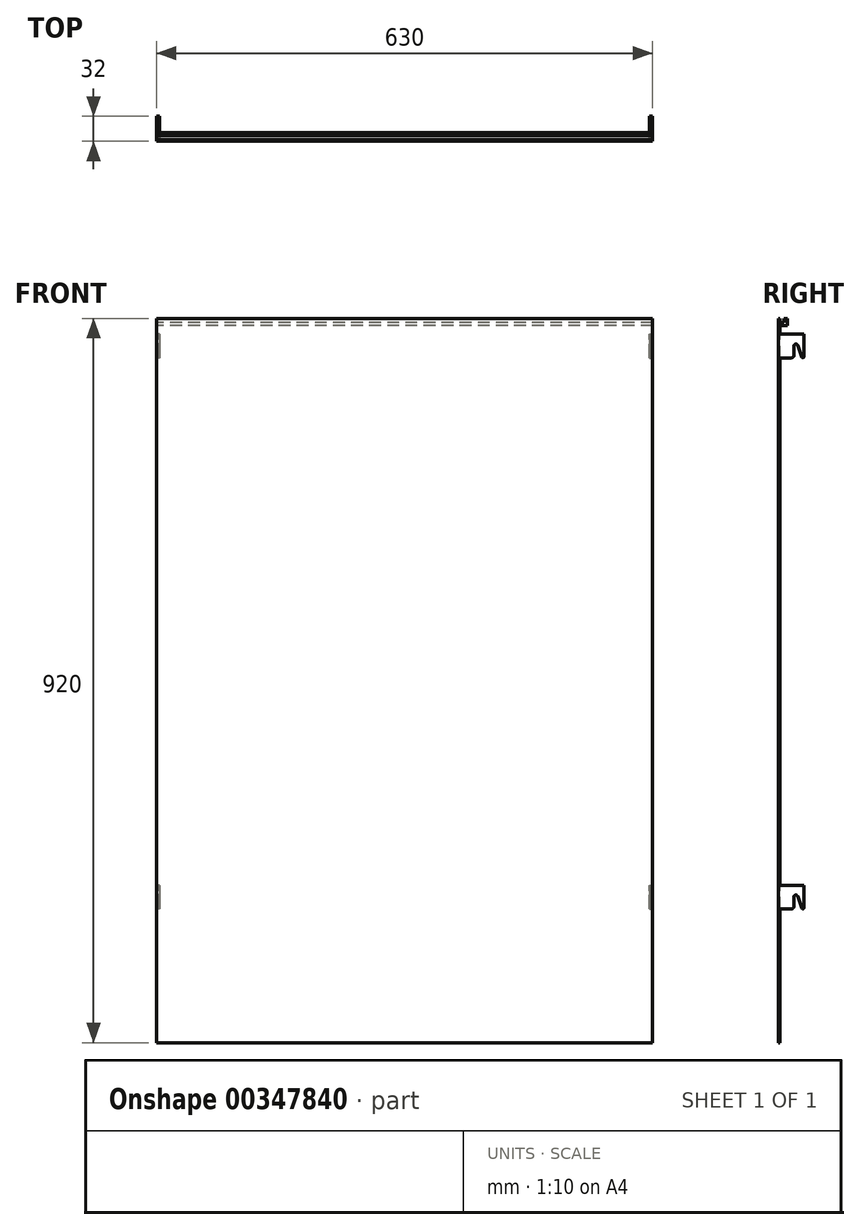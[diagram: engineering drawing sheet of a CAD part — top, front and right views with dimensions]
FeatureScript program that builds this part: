
annotation { "Feature Type Name" : "Feature", "Feature Type Description" : "" }
export const myFeature = defineFeature(function(context is Context, id is Id, definition is map)
    precondition{}
    {
        {
            var Q0;
            Q0=qCreatedBy(makeId("Front.planeOp"),FACE);
            var sketch = newSketch(context, id + "F0", { "sketchPlane" : qUnion([Q0])});
            skLineSegment(sketch, "E0.bottom", {"start": v(315, -460) * mm, "end": v(-315, -460) * mm});
            skLineSegment(sketch, "E0.top", {"start": v(315, 460) * mm, "end": v(-315, 460) * mm});
            skLineSegment(sketch, "E0.left", {"start": v(315, -460) * mm, "end": v(315, 460) * mm});
            skLineSegment(sketch, "E0.right", {"start": v(-315, -460) * mm, "end": v(-315, 460) * mm});
            skPoint(sketch, "E0.middle", {"position": v(0, 0) * mm});
            skLineSegment(sketch, "E1.0", {"start": v(315, 455) * mm, "end": v(-315, 455) * mm});
            skLineSegment(sketch, "E2.0", {"start": v(315, 451) * mm, "end": v(-315, 451) * mm});
            skSolve(sketch);
        }
        {
            var Q0;
            Q0=makeQuery(id+"F0.imprint","IMPRINT",FACE,{"disambiguationData":[TD([[makeQuery(id+"F0.imprint","IMPRINT",EDGE,{"derivedFrom":sQuery(id+"F0.wireOp",EDGE,"E0.bottom")}),-1.0]])]});
            var Q1;
            {var subQ0=sQuery(id+"F0.wireOp",EDGE,"E1.0");Q1=makeQuery(id+"F0.imprint","IMPRINT",FACE,{"disambiguationData":[TD([[makeQuery(id+"F0.imprint","IMPRINT",EDGE,{"derivedFrom":subQ0}),1.0]])]});}
            var Q2;
            {var subQ0=sQuery(id+"F0.wireOp",EDGE,"E0.top");Q2=makeQuery(id+"F0.imprint","IMPRINT",FACE,{"disambiguationData":[TD([[makeQuery(id+"F0.imprint","IMPRINT",EDGE,{"derivedFrom":subQ0}),1.0]])]});}
            extrude(context, id + "F1", {"entities" : qUnion([Q0, Q1, Q2]), "depth" : 2 * mm});
        }
        {
            var Q0;
            Q0=qCreatedBy(makeId("Right.planeOp"),FACE);
            cPlane(context, id + "F2", {"entities" : qUnion([Q0]), "cplaneType" : CPlaneType.OFFSET, "offset" : 315 * mm, "oppositeDirection" : true, "width" : 150 * mm, "height" : 150 * mm});
        }
        {
            var Q0;
            Q0=qCreatedBy(id+"F2.planeOp",FACE);
            var sketch = newSketch(context, id + "F3", { "sketchPlane" : qUnion([Q0])});
            skLineSegment(sketch, "E3", {"start": v(0, 0) * mm, "end": v(0, 440) * mm});
            skLineSegment(sketch, "E4", {"start": v(0, 440) * mm, "end": v(30, 440) * mm});
            skLineSegment(sketch, "E5", {"start": v(30, 440) * mm, "end": v(30, 410.95) * mm});
            skLineSegment(sketch, "E6", {"start": v(29.05, 410) * mm, "end": v(28.67, 410) * mm});
            skLineSegment(sketch, "E7", {"start": v(28, 410) * mm, "end": v(20, 410) * mm});
            skLineSegment(sketch, "E8", {"start": v(20, 410) * mm, "end": v(20, 425) * mm});
            skCircle(sketch, "E9", {"center": v(20, 425) * mm, "radius": 2.5 * mm});
            skLineSegment(sketch, "E10", {"start": v(27.77, 410.63) * mm, "end": v(22.35, 425.84) * mm});
            skLineSegment(sketch, "E11", {"start": v(17.5, 425) * mm, "end": v(17.5, 413) * mm});
            skLineSegment(sketch, "E12", {"start": v(14.5, 410) * mm, "end": v(0, 410) * mm});
            skPoint(sketch, "E13.visualSharp", {"position": v(17.5, 410) * mm});
            skArc(sketch, "E13.filletArc", {"start": v(14.5, 410) * mm, "mid": v(16.62, 410.88) * mm, "end": v(17.5, 413) * mm});
            skPoint(sketch, "E14.visualSharp", {"position": v(28, 410) * mm});
            skArc(sketch, "E14.filletArc", {"start": v(27.77, 410.63) * mm, "mid": v(28.12, 410.17) * mm, "end": v(28.67, 410) * mm});
            skPoint(sketch, "E15.visualSharp", {"position": v(30, 410) * mm});
            skArc(sketch, "E15.filletArc", {"start": v(29.05, 410) * mm, "mid": v(29.72, 410.28) * mm, "end": v(30, 410.95) * mm});
            skSolve(sketch);
        }
        {
            var Q0;
            {var subQ4=sQuery(id+"F3.wireOp",EDGE,"E4");Q0=makeQuery(id+"F3.imprint","IMPRINT",FACE,{"disambiguationData":[TD([[makeQuery(id+"F3.imprint","IMPRINT",EDGE,{"derivedFrom":subQ4}),-1.0]])]});}
            extrude(context, id + "F4", {"entities" : qUnion([Q0]), "depth" : 4 * mm});
        }
        {
            var Q0;
            Q0=makeQuery(id+"F4.opExtrude","SWEPT_BODY",BODY,{"disambiguationData":[OSD([sQuery(id+"F3.wireOp",EDGE,"E3"),sQuery(id+"F3.wireOp",EDGE,"E4"),sQuery(id+"F3.wireOp",EDGE,"E5"),sQuery(id+"F3.wireOp",EDGE,"E6"),sQuery(id+"F3.wireOp",EDGE,"E9"),sQuery(id+"F3.wireOp",EDGE,"E10"),sQuery(id+"F3.wireOp",EDGE,"E11"),sQuery(id+"F3.wireOp",EDGE,"E12"),sQuery(id+"F3.wireOp",EDGE,"E13.filletArc"),sQuery(id+"F3.wireOp",EDGE,"E14.filletArc"),sQuery(id+"F3.wireOp",EDGE,"E15.filletArc")])]});
            transform(context, id + "F5", {"entities" : qUnion([Q0]), "transformType" : TransformType.TRANSLATION_3D, "dx" : 0 * mm, "dy" : 0 * mm, "dz" : -700 * mm, "makeCopy" : true});
        }
        {
            var Q0;
            Q0=makeQuery(id+"F4.opExtrude","SWEPT_BODY",BODY,{"disambiguationData":[OSD([sQuery(id+"F3.wireOp",EDGE,"E3"),sQuery(id+"F3.wireOp",EDGE,"E4"),sQuery(id+"F3.wireOp",EDGE,"E5"),sQuery(id+"F3.wireOp",EDGE,"E6"),sQuery(id+"F3.wireOp",EDGE,"E9"),sQuery(id+"F3.wireOp",EDGE,"E10"),sQuery(id+"F3.wireOp",EDGE,"E11"),sQuery(id+"F3.wireOp",EDGE,"E12"),sQuery(id+"F3.wireOp",EDGE,"E13.filletArc"),sQuery(id+"F3.wireOp",EDGE,"E14.filletArc"),sQuery(id+"F3.wireOp",EDGE,"E15.filletArc")])]});
            var Q1;
            Q1=makeQuery(id+"F5.opPattern","COPY",BODY,{"derivedFrom":makeQuery(id+"F4.opExtrude","SWEPT_BODY",BODY,{"disambiguationData":[OSD([sQuery(id+"F3.wireOp",EDGE,"E3"),sQuery(id+"F3.wireOp",EDGE,"E4"),sQuery(id+"F3.wireOp",EDGE,"E5"),sQuery(id+"F3.wireOp",EDGE,"E6"),sQuery(id+"F3.wireOp",EDGE,"E9"),sQuery(id+"F3.wireOp",EDGE,"E10"),sQuery(id+"F3.wireOp",EDGE,"E11"),sQuery(id+"F3.wireOp",EDGE,"E12"),sQuery(id+"F3.wireOp",EDGE,"E13.filletArc"),sQuery(id+"F3.wireOp",EDGE,"E14.filletArc"),sQuery(id+"F3.wireOp",EDGE,"E15.filletArc")])]}),"instanceName":"1"});
            var Q2;
            Q2=qCreatedBy(makeId("Right.planeOp"),FACE);
            mirror(context, id + "F6", {"operationType" : NewBodyOperationType.ADD, "entities" : qUnion([Q0, Q1]), "mirrorPlane" : qUnion([Q2])});
        }
        {
            var Q0;
            {var subQ0=sQuery(id+"F0.wireOp",EDGE,"E1.0");Q0=makeQuery(id+"F0.imprint","IMPRINT",FACE,{"disambiguationData":[TD([[makeQuery(id+"F0.imprint","IMPRINT",EDGE,{"derivedFrom":subQ0}),1.0]])]});}
            extrude(context, id + "F7", {"entities" : qUnion([Q0]), "operationType" : NewBodyOperationType.ADD, "oppositeDirection" : true, "depth" : 9 * mm});
        }
        {
            var Q0;
            Q0=makeQuery(id+"F7.opExtrude","SWEPT_FACE",FACE,{"disambiguationData":[OSD([sQuery(id+"F0.wireOp",EDGE,"E1.0")])]});
            var sketch = newSketch(context, id + "F8", { "sketchPlane" : qUnion([Q0])});
            skLineSegment(sketch, "E16.bottom", {"start": v(315, 9) * mm, "end": v(-315, 9) * mm});
            skLineSegment(sketch, "E16.top", {"start": v(315, 5) * mm, "end": v(-315, 5) * mm});
            skLineSegment(sketch, "E16.left", {"start": v(315, 9) * mm, "end": v(315, 5) * mm});
            skLineSegment(sketch, "E16.right", {"start": v(-315, 9) * mm, "end": v(-315, 5) * mm});
            skSolve(sketch);
        }
        {
            var Q0;
            Q0=makeQuery(id+"F8.imprint","IMPRINT",FACE,{"disambiguationData":[TD([[makeQuery(id+"F8.imprint","IMPRINT",EDGE,{"derivedFrom":sQuery(id+"F8.wireOp",EDGE,"E16.bottom")}),1.0]])]});
            extrude(context, id + "F9", {"entities" : qUnion([Q0]), "operationType" : NewBodyOperationType.ADD, "depth" : 5 * mm});
        }
    });
